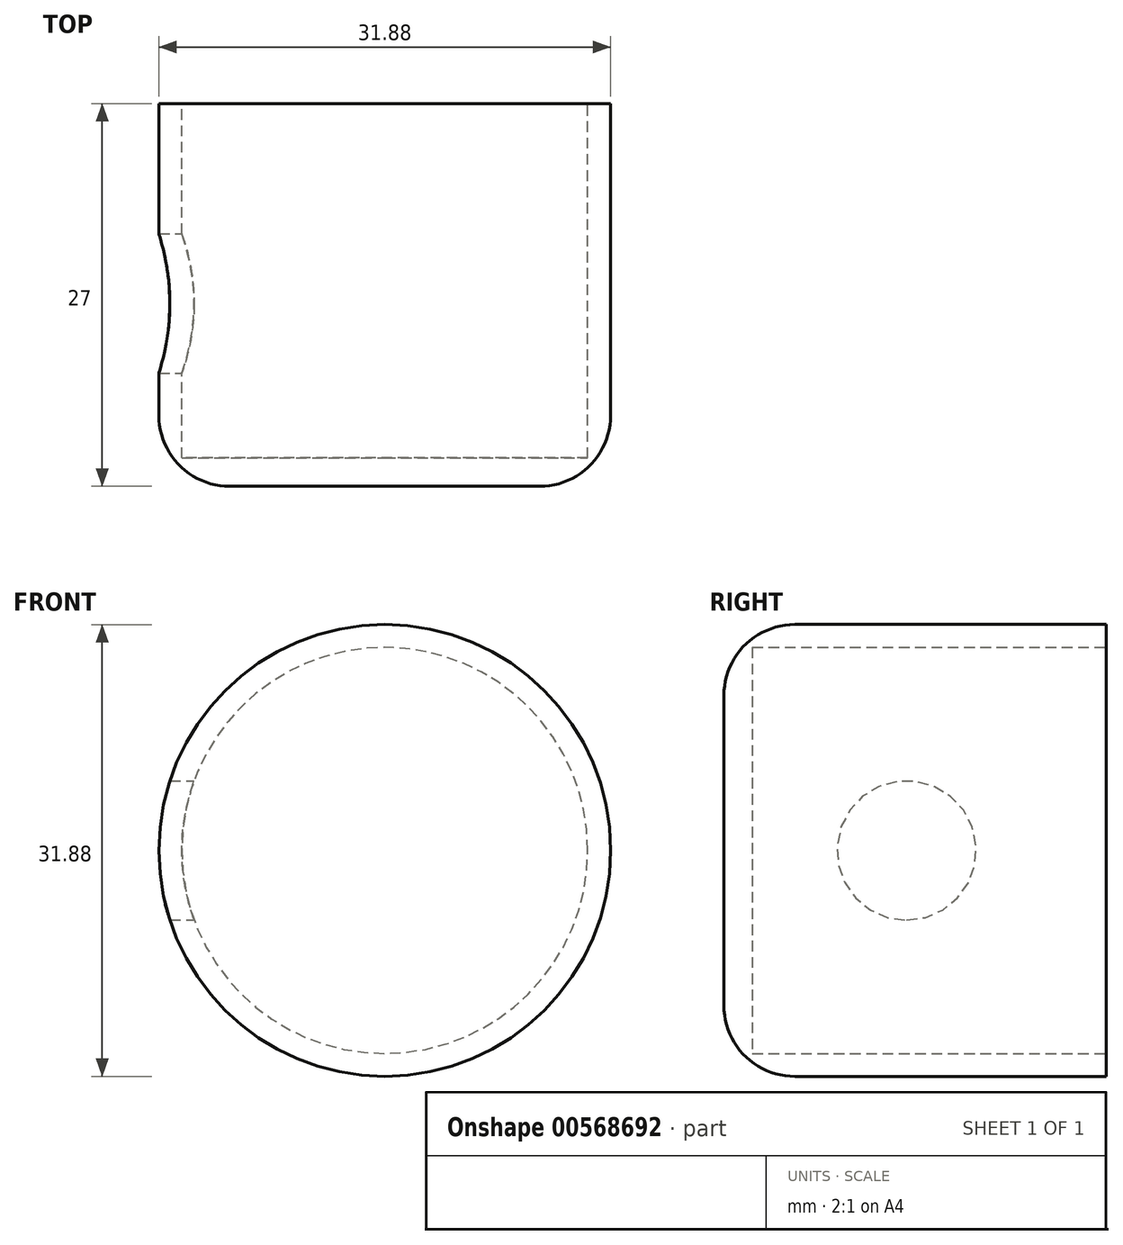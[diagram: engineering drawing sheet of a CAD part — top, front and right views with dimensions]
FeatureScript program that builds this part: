
annotation { "Feature Type Name" : "Feature", "Feature Type Description" : "" }
export const myFeature = defineFeature(function(context is Context, id is Id, definition is map)
    precondition{}
    {
        {
            var Q0;
            Q0=qCreatedBy(makeId("Front.planeOp"),FACE);
            var sketch = newSketch(context, id + "F0", { "sketchPlane" : qUnion([Q0])});
            skCircle(sketch, "E0", {"center": v(0, 0) * mm, "radius": 15.94 * mm});
            skSolve(sketch);
        }
        {
            var Q0;
            Q0=makeQuery(id+"F0.imprint","IMPRINT",FACE,{"disambiguationData":[TD([[makeQuery(id+"F0.imprint","IMPRINT",EDGE,{"derivedFrom":sQuery(id+"F0.wireOp",EDGE,"E0")}),1.0]])]});
            var Q1;
            Q1=sQuery(id+"F0.wireOp",EDGE,"E0");
            extrude(context, id + "F1", {"entities" : qUnion([Q0]), "surfaceEntities" : qUnion([Q1]), "depth" : 12 * mm, "offsetDistance" : 25 * mm});
        }
        {
            var Q0;
            Q0=makeQuery(id+"F1.opExtrude","CAP_FACE",FACE,{"disambiguationData":[OSD([sQuery(id+"F0.wireOp",EDGE,"E0")])],"isStart":true});
            extrude(context, id + "F2", {"entities" : qUnion([Q0]), "operationType" : NewBodyOperationType.ADD, "depth" : 15 * mm, "offsetDistance" : 25 * mm});
        }
        {
            var Q0;
            Q0=makeQuery(id+"F2.opExtrude","CAP_FACE",FACE,{"disambiguationData":[OSD([sQuery(id+"F0.wireOp",EDGE,"E0")])],"isStart":false});
            var sketch = newSketch(context, id + "F3", { "sketchPlane" : qUnion([Q0])});
            skCircle(sketch, "E1", {"center": v(0, 0) * mm, "radius": 14.32 * mm});
            skSolve(sketch);
        }
        {
            var Q0;
            Q0=makeQuery(id+"F3.imprint","IMPRINT",FACE,{"disambiguationData":[TD([[makeQuery(id+"F3.imprint","IMPRINT",EDGE,{"derivedFrom":sQuery(id+"F3.wireOp",EDGE,"E1")}),1.0]])]});
            extrude(context, id + "F4", {"entities" : qUnion([Q0]), "operationType" : NewBodyOperationType.REMOVE, "oppositeDirection" : true, "depth" : 25 * mm, "offsetDistance" : 25 * mm});
        }
        {
            var Q0;
            Q0=makeQuery(id+"F1.opExtrude","CAP_EDGE",EDGE,{"disambiguationData":[OSD([sQuery(id+"F0.wireOp",EDGE,"E0")])],"isStart":false});
            fillet(context, id + "F5", {"entities" : qUnion([Q0]), "radius" : 5 * mm, "tangentPropagation" : true, "allowEdgeOverflow" : false});
        }
        {
            var Q0;
            Q0=qCreatedBy(makeId("Right.planeOp"),FACE);
            var sketch = newSketch(context, id + "F6", { "sketchPlane" : qUnion([Q0])});
            skCircle(sketch, "E2", {"center": v(0.9, 0) * mm, "radius": 4.91 * mm});
            skSolve(sketch);
        }
        {
            var Q0;
            Q0=makeQuery(id+"F6.imprint","IMPRINT",FACE,{"disambiguationData":[TD([[makeQuery(id+"F6.imprint","IMPRINT",EDGE,{"derivedFrom":sQuery(id+"F6.wireOp",EDGE,"E2")}),1.0]])]});
            extrude(context, id + "F7", {"entities" : qUnion([Q0]), "operationType" : NewBodyOperationType.REMOVE, "endBound" : BoundingType.THROUGH_ALL, "oppositeDirection" : true, "depth" : 6 * mm, "offsetDistance" : 25 * mm});
        }
    });
